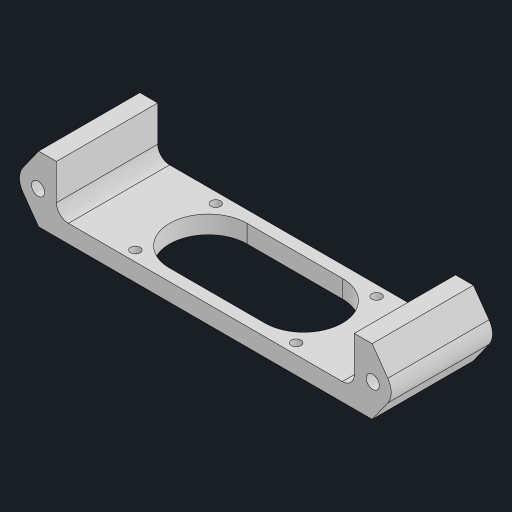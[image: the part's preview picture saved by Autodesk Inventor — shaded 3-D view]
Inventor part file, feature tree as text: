
AUTODESK INVENTOR PART (.ipt)
format: ipt  version: 2023 (Build 270158000, 158)  size: 161,792 bytes
history: native  units: mm
features: sketch x2, extrude x2, other x1, hole x1, fillet x1, mirror x1
ambient origin geometry x8: Origin, YZ Plane, XZ Plane, XY Plane, X Axis, Y Axis, Z Axis, Center Point
bodies: Body1 (feature_tree)
feature tree (8):
  other  "ソリッド1"
  sketch  "スケッチ1"
  extrude  "押し出し1"  Depth=13.5mm
  hole  "穴1"  [1 undecoded]
  extrude  "押し出し2"  Depth=8.0mm
  fillet  "フィレット1"  Radius=13.0mm
  mirror  "ミラー1"
  sketch  "スケッチ2"
note: 1 required parameter value undecoded (feature->parameter linkage not recoverable at this tier; creation-order binding heuristic only, values carry confidence <= 0.55)
